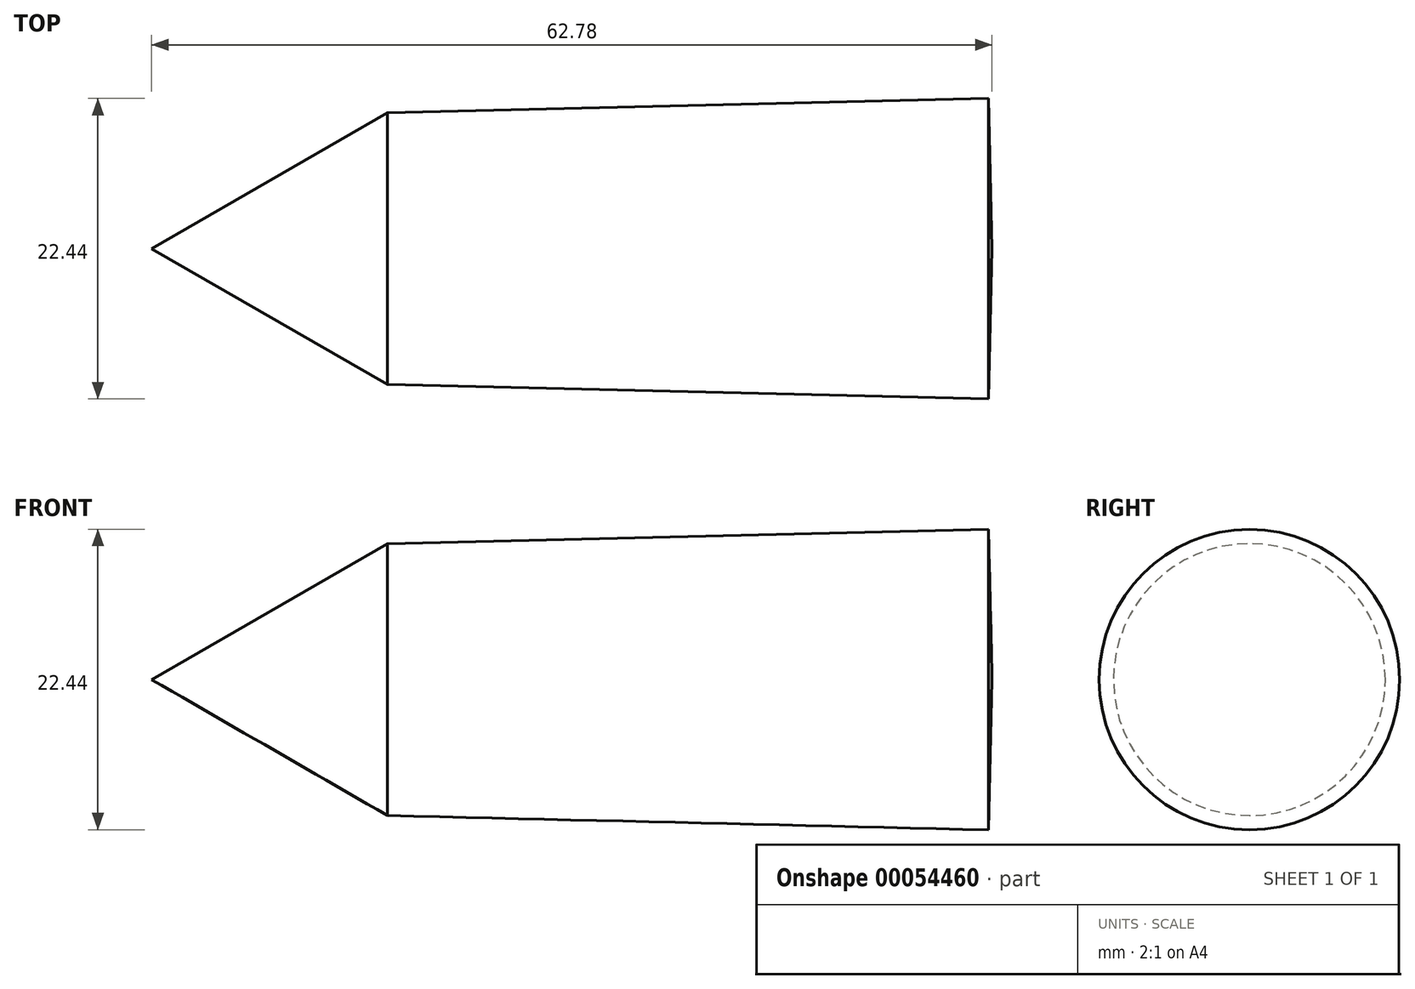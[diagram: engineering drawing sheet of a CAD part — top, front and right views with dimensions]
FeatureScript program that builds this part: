
annotation { "Feature Type Name" : "Feature", "Feature Type Description" : "" }
export const myFeature = defineFeature(function(context is Context, id is Id, definition is map)
    precondition{}
    {
        {
            var Q0;
            Q0=qCreatedBy(makeId("Front.planeOp"),FACE);
            var sketch = newSketch(context, id + "F0", { "sketchPlane" : qUnion([Q0])});
            skLineSegment(sketch, "E0", {"start": v(-17.63, -0.13) * mm, "end": v(0, 10.02) * mm});
            skLineSegment(sketch, "E1", {"start": v(0, 10.02) * mm, "end": v(44.88, 11.09) * mm});
            skLineSegment(sketch, "E2", {"start": v(44.88, 11.09) * mm, "end": v(45.15, -0.13) * mm});
            skLineSegment(sketch, "E3", {"start": v(45.15, -0.13) * mm, "end": v(-17.9, -0.13) * mm});
            skSolve(sketch);
        }
        {
            var Q0;
            Q0 = qSketchRegion(id + "F0", true);
            var Q1;
            Q1=sQuery(id+"F0.wireOp",EDGE,"E3");
            revolve(context, id + "F1", {"entities" : qUnion([Q0]), "axis" : qUnion([Q1]), "revolveType" : RevolveType.FULL});
        }
    });
